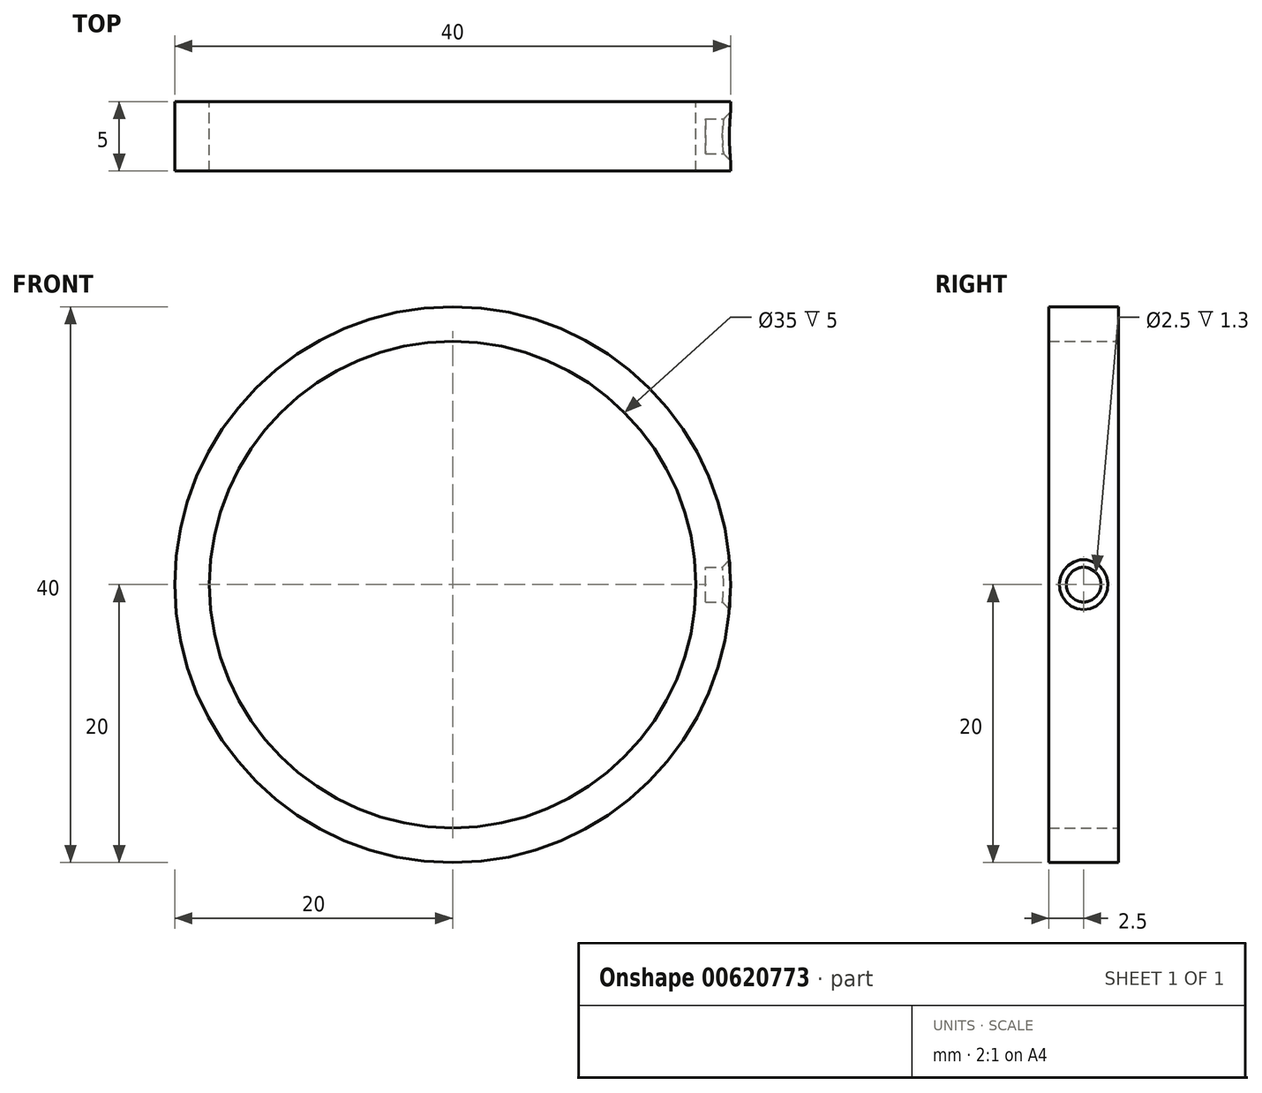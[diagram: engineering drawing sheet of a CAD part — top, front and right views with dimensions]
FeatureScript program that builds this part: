
annotation { "Feature Type Name" : "Feature", "Feature Type Description" : "" }
export const myFeature = defineFeature(function(context is Context, id is Id, definition is map)
    precondition{}
    {
        {
            var Q0;
            Q0=qCreatedBy(makeId("Front.planeOp"),FACE);
            var sketch = newSketch(context, id + "F0", { "sketchPlane" : qUnion([Q0])});
            skCircle(sketch, "E0", {"center": v(0, 0) * mm, "radius": 20 * mm});
            skCircle(sketch, "E1", {"center": v(0, 0) * mm, "radius": 17.5 * mm});
            skSolve(sketch);
        }
        {
            var Q0;
            Q0 = qSketchRegion(id + "F0", true);
            extrude(context, id + "F1", {"entities" : qUnion([Q0]), "depth" : 5 * mm, "offsetDistance" : 25 * mm});
        }
        {
            var Q0;
            Q0=qCreatedBy(makeId("Right.planeOp"),FACE);
            cPlane(context, id + "F2", {"entities" : qUnion([Q0]), "cplaneType" : CPlaneType.OFFSET, "offset" : 20.7 * mm, "width" : 150 * mm, "height" : 150 * mm});
        }
        {
            var Q0;
            Q0=qCreatedBy(id+"F2.planeOp",FACE);
            var sketch = newSketch(context, id + "F3", { "sketchPlane" : qUnion([Q0])});
            skCircle(sketch, "E2", {"center": v(-2.5, 0) * mm, "radius": 1.25 * mm});
            skSolve(sketch);
        }
        {
            var Q0;
            Q0 = qSketchRegion(id + "F3", true);
            extrude(context, id + "F4", {"entities" : qUnion([Q0]), "operationType" : NewBodyOperationType.REMOVE, "oppositeDirection" : true, "depth" : 2.5 * mm, "offsetDistance" : 25 * mm});
        }
        {
            var Q0;
            Q0=makeQuery(id+"F4.boolean.opBoolean","INTERSECT",EDGE,{"derivedFrom":[makeQuery(id+"F1.opExtrude","SWEPT_FACE",FACE,{"disambiguationData":[OSD([sQuery(id+"F0.wireOp",EDGE,"E0")])]}),makeQuery(id+"F4.opExtrude","SWEPT_FACE",FACE,{"disambiguationData":[OSD([sQuery(id+"F3.wireOp",EDGE,"E2")])]})]});
            var Q1;
            Q1=makeQuery(id+"F7CZBdJCqOUOP4b_1.1.F4.boolean.opBoolean","INTERSECT",EDGE,{"derivedFrom":[makeQuery(id+"F1.opExtrude","SWEPT_FACE",FACE,{"disambiguationData":[OSD([sQuery(id+"F0.wireOp",EDGE,"E0")])]}),makeQuery(id+"F7CZBdJCqOUOP4b_1.1.F4.opExtrude","SWEPT_FACE",FACE,{"disambiguationData":[OSD([sQuery(id+"F3.wireOp",EDGE,"E2")])]})]});
            chamfer(context, id + "F5", {"entities" : qUnion([Q0, Q1]), "width" : 0.5 * mm, "tangentPropagation" : true});
        }
    });
